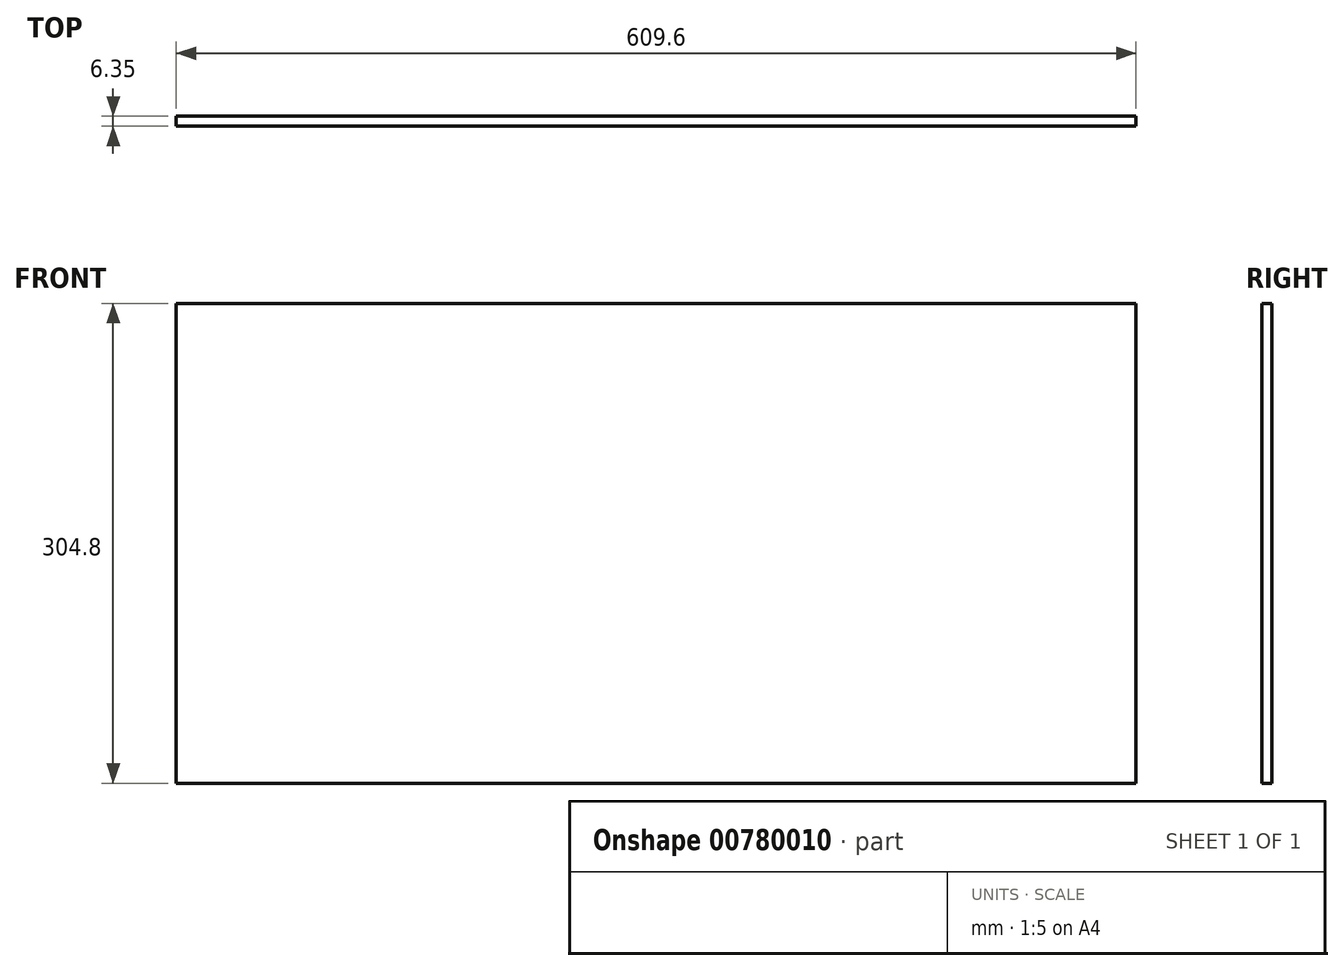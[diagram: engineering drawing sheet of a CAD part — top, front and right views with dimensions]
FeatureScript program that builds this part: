
annotation { "Feature Type Name" : "Feature", "Feature Type Description" : "" }
export const myFeature = defineFeature(function(context is Context, id is Id, definition is map)
    precondition{}
    {
        {
            var Q0;
            Q0=qCreatedBy(makeId("Front.planeOp"),FACE);
            var sketch = newSketch(context, id + "F0", { "sketchPlane" : qUnion([Q0])});
            skLineSegment(sketch, "E0.bottom", {"start": v(0, 0) * mm, "end": v(609.6, 0) * mm});
            skLineSegment(sketch, "E0.top", {"start": v(0, 304.8) * mm, "end": v(609.6, 304.8) * mm});
            skLineSegment(sketch, "E0.left", {"start": v(0, 0) * mm, "end": v(0, 304.8) * mm});
            skLineSegment(sketch, "E0.right", {"start": v(609.6, 0) * mm, "end": v(609.6, 304.8) * mm});
            skSolve(sketch);
        }
        {
            var Q0;
            Q0 = qSketchRegion(id + "F0", true);
            extrude(context, id + "F1", {"entities" : qUnion([Q0]), "depth" : 6.35 * mm, "offsetDistance" : 25.4 * mm});
        }
    });
